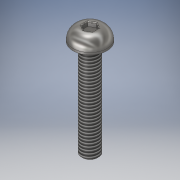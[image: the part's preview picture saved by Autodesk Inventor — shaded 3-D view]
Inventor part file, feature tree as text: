
AUTODESK INVENTOR PART (.ipt)
format: ipt  version: 2018 (Build 220112000, 112)  size: 215,552 bytes
history: native  units: in
note: dims shown in document units (in); Inventor stores cm internally (conversion verified against a paired STEP export)
features: extrude x3, sketch x3, fillet x2, chamfer x1, thread x1
ambient origin geometry x8: Origin, YZ Plane, XZ Plane, XY Plane, X Axis, Y Axis, Z Axis, Center Point
bodies: Solid1 (feature_tree)
feature tree (10):
  extrude  "Extrusion1"  Depth=0.1181in TaperAngle=0.0deg
  fillet  "Fillet1"  Radius=0.0984in
  extrude  "Extrusion2"  Depth=0.0079in
  fillet  "Fillet2"  Radius=0.1575in
  extrude  "Extrusion3"  Depth=0.0787in TaperAngle=45.0deg
  chamfer  "Chamfer1"  Distance=0.3937in
  thread  "Thread1"  [1 undecoded]
  sketch  "Sketch1"  dims[d0=0.315in d1=0.1181in d2=0.0in d3=0.0984in]
  sketch  "Sketch2"  dims[d4=0.0394in d5=0.0in d6=0.0079in d7=0.1575in]
  sketch  "Sketch3"  dims[d8=0.9055in d9=0.0in d10=0.0098in d11=0.0787in d12=45.0deg d13=0.3937in d14=0.0in]
note: 1 required parameter value undecoded (feature->parameter linkage not recoverable at this tier; creation-order binding heuristic only, values carry confidence <= 0.55)
